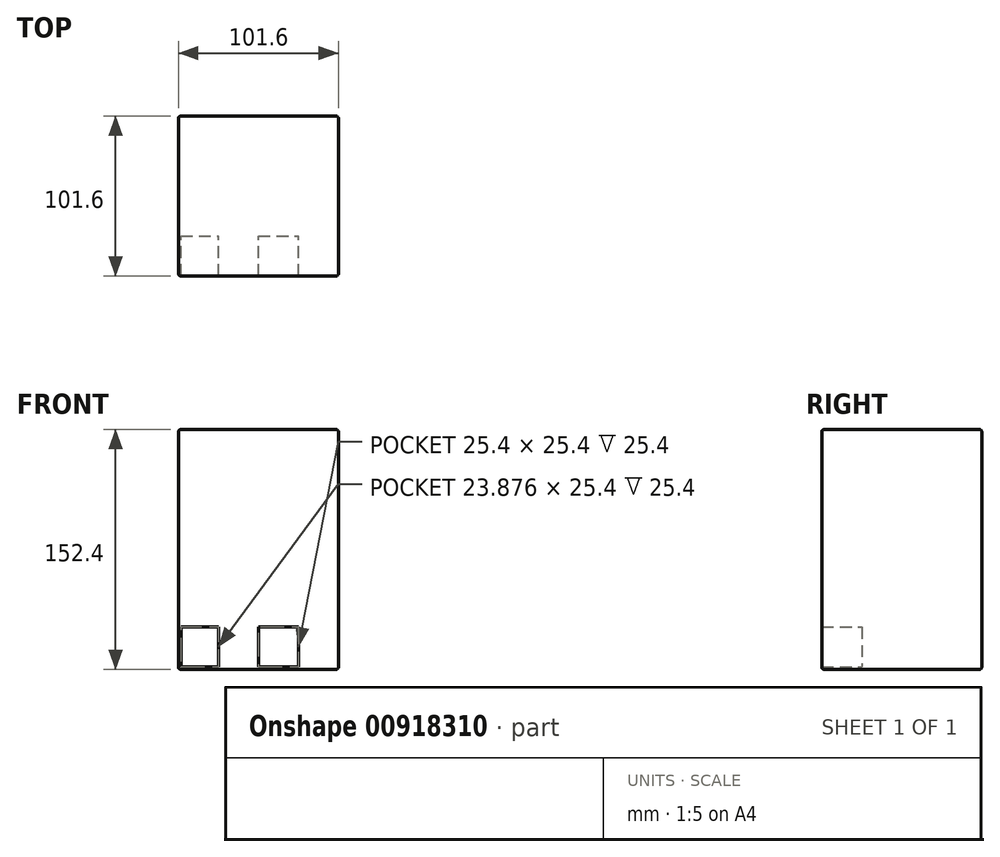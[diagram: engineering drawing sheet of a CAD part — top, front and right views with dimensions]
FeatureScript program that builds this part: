
annotation { "Feature Type Name" : "Feature", "Feature Type Description" : "" }
export const myFeature = defineFeature(function(context is Context, id is Id, definition is map)
    precondition{}
    {
        {
            var Q0;
            Q0=qCreatedBy(makeId("Top.planeOp"),FACE);
            var sketch = newSketch(context, id + "F0", { "sketchPlane" : qUnion([Q0])});
            skLineSegment(sketch, "E0.bottom", {"start": v(50.8, 50.8) * mm, "end": v(-50.8, 50.8) * mm});
            skLineSegment(sketch, "E0.top", {"start": v(50.8, -50.8) * mm, "end": v(-50.8, -50.8) * mm});
            skLineSegment(sketch, "E0.left", {"start": v(50.8, 50.8) * mm, "end": v(50.8, -50.8) * mm});
            skLineSegment(sketch, "E0.right", {"start": v(-50.8, 50.8) * mm, "end": v(-50.8, -50.8) * mm});
            skPoint(sketch, "E0.middle", {"position": v(0, 0) * mm});
            skSolve(sketch);
        }
        {
            var Q0;
            Q0=makeQuery(id+"F0.imprint","IMPRINT",FACE,{"disambiguationData":[TD([[makeQuery(id+"F0.imprint","IMPRINT",EDGE,{"derivedFrom":sQuery(id+"F0.wireOp",EDGE,"E0.bottom")}),1.0]])]});
            extrude(context, id + "F1", {"entities" : qUnion([Q0]), "depth" : 152.4 * mm, "offsetDistance" : 25.4 * mm});
        }
        {
            var Q0;
            Q0=makeQuery(id+"F1.opExtrude","SWEPT_FACE",FACE,{"disambiguationData":[OSD([sQuery(id+"F0.wireOp",EDGE,"E0.top")])]});
            var Q1;
            Q1=makeQuery(id+"F1.opExtrude","SWEPT_FACE",FACE,{"disambiguationData":[OSD([sQuery(id+"F0.wireOp",EDGE,"E0.bottom")])]});
            var Q2;
            Q2=makeQuery(id+"F1.opExtrude","CAP_FACE",FACE,{"disambiguationData":[OSD([sQuery(id+"F0.wireOp",EDGE,"E0.bottom"),sQuery(id+"F0.wireOp",EDGE,"E0.top"),sQuery(id+"F0.wireOp",EDGE,"E0.left"),sQuery(id+"F0.wireOp",EDGE,"E0.right")])],"isStart":false});
            var Q3;
            Q3=makeQuery(id+"F1.opExtrude","CAP_FACE",FACE,{"disambiguationData":[OSD([sQuery(id+"F0.wireOp",EDGE,"E0.bottom"),sQuery(id+"F0.wireOp",EDGE,"E0.top"),sQuery(id+"F0.wireOp",EDGE,"E0.left"),sQuery(id+"F0.wireOp",EDGE,"E0.right")])],"isStart":true});
            fillet(context, id + "F2", {"entities" : qUnion([Q0, Q1, Q2, Q3]), "radius" : 1.52 * mm, "tangentPropagation" : true, "allowEdgeOverflow" : false});
        }
        {
            var Q0;
            Q0=makeQuery(id+"F1.opExtrude","SWEPT_FACE",FACE,{"disambiguationData":[OSD([sQuery(id+"F0.wireOp",EDGE,"E0.top")])]});
            var sketch = newSketch(context, id + "F3", { "sketchPlane" : qUnion([Q0])});
            skLineSegment(sketch, "E1.bottom", {"start": v(-49.28, 1.52) * mm, "end": v(-25.4, 1.52) * mm});
            skLineSegment(sketch, "E1.top", {"start": v(-49.28, 26.92) * mm, "end": v(-25.4, 26.92) * mm});
            skLineSegment(sketch, "E1.left", {"start": v(-49.28, 1.52) * mm, "end": v(-49.28, 26.92) * mm});
            skLineSegment(sketch, "E1.right", {"start": v(-25.4, 1.52) * mm, "end": v(-25.4, 26.92) * mm});
            skLineSegment(sketch, "E2.bottom", {"start": v(-25.4, 26.92) * mm, "end": v(0, 26.92) * mm});
            skLineSegment(sketch, "E2.top", {"start": v(-25.4, 1.52) * mm, "end": v(0, 1.52) * mm});
            skLineSegment(sketch, "E2.left", {"start": v(-25.4, 26.92) * mm, "end": v(-25.4, 1.52) * mm});
            skLineSegment(sketch, "E2.right", {"start": v(0, 26.92) * mm, "end": v(0, 1.52) * mm});
            skLineSegment(sketch, "E3.bottom", {"start": v(0, 26.92) * mm, "end": v(25.4, 26.92) * mm});
            skLineSegment(sketch, "E3.top", {"start": v(0, 1.52) * mm, "end": v(25.4, 1.52) * mm});
            skLineSegment(sketch, "E3.right", {"start": v(25.4, 26.92) * mm, "end": v(25.4, 1.52) * mm});
            skLineSegment(sketch, "E4.bottom", {"start": v(25.4, 26.92) * mm, "end": v(49.28, 26.92) * mm});
            skLineSegment(sketch, "E4.top", {"start": v(25.4, 1.52) * mm, "end": v(49.28, 1.52) * mm});
            skLineSegment(sketch, "E4.right", {"start": v(49.28, 26.92) * mm, "end": v(49.28, 1.52) * mm});
            skSolve(sketch);
        }
        {
            var Q0;
            Q0=makeQuery(id+"F3.imprint","IMPRINT",FACE,{"disambiguationData":[TD([[makeQuery(id+"F3.imprint","IMPRINT",EDGE,{"derivedFrom":sQuery(id+"F3.wireOp",EDGE,"E1.bottom")}),1.0]])]});
            var Q1;
            Q1=makeQuery(id+"F3.imprint","IMPRINT",FACE,{"disambiguationData":[TD([[makeQuery(id+"F3.imprint","IMPRINT",EDGE,{"derivedFrom":sQuery(id+"F3.wireOp",EDGE,"E3.bottom")}),-1.0]])]});
            extrude(context, id + "F4", {"entities" : qUnion([Q0, Q1]), "operationType" : NewBodyOperationType.REMOVE, "oppositeDirection" : true, "depth" : 25.4 * mm, "offsetDistance" : 25.4 * mm});
        }
        {
            var Q0;
            Q0=makeQuery(id+"F4.boolean.opBoolean","COPY",FACE,{"derivedFrom":makeQuery(id+"F4.opExtrude","CAP_FACE",FACE,{"disambiguationData":[OSD([sQuery(id+"F3.wireOp",EDGE,"E3.bottom"),sQuery(id+"F3.wireOp",EDGE,"E3.top"),sQuery(id+"F3.wireOp",EDGE,"E2.right"),sQuery(id+"F3.wireOp",EDGE,"E3.right")])],"isStart":false})});
            var Q1;
            Q1=makeQuery(id+"F4.boolean.opBoolean","COPY",FACE,{"derivedFrom":makeQuery(id+"F4.opExtrude","CAP_FACE",FACE,{"disambiguationData":[OSD([sQuery(id+"F3.wireOp",EDGE,"E1.bottom"),sQuery(id+"F3.wireOp",EDGE,"E1.top"),sQuery(id+"F3.wireOp",EDGE,"E1.left"),sQuery(id+"F3.wireOp",EDGE,"E2.left")])],"isStart":false})});
            extrude(context, id + "F5", {"entities" : qUnion([Q0, Q1]), "depth" : 25.4 * mm, "offsetDistance" : 25.4 * mm});
        }
    });
